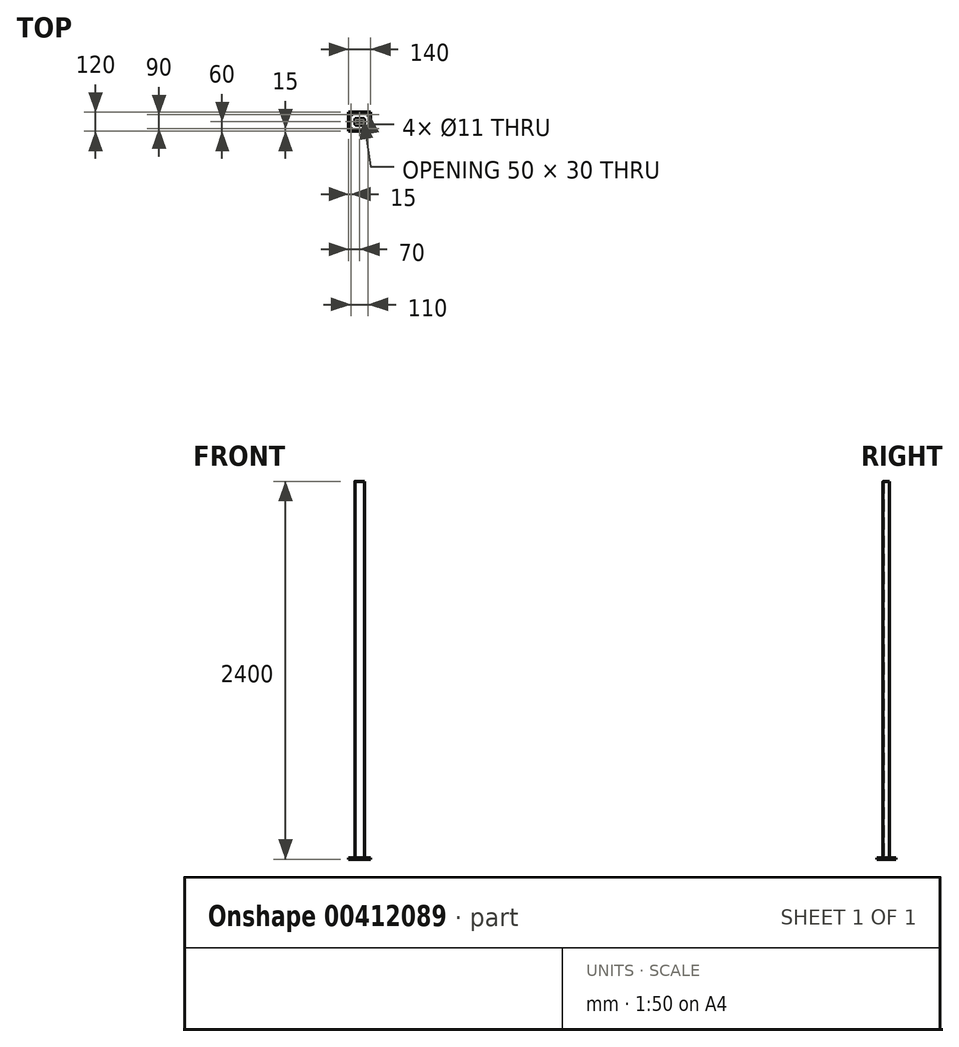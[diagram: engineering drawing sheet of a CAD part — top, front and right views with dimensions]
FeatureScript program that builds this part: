
annotation { "Feature Type Name" : "Feature", "Feature Type Description" : "" }
export const myFeature = defineFeature(function(context is Context, id is Id, definition is map)
    precondition{}
    {
        {
            var Q0;
            Q0=qCreatedBy(makeId("Top.planeOp"),FACE);
            var sketch = newSketch(context, id + "F0", { "sketchPlane" : qUnion([Q0])});
            skLineSegment(sketch, "E0.bottom", {"start": v(-70, 60) * mm, "end": v(70, 60) * mm});
            skLineSegment(sketch, "E0.top", {"start": v(-70, -60) * mm, "end": v(70, -60) * mm});
            skLineSegment(sketch, "E0.left", {"start": v(-70, 60) * mm, "end": v(-70, -60) * mm});
            skLineSegment(sketch, "E0.right", {"start": v(70, 60) * mm, "end": v(70, -60) * mm});
            skCircle(sketch, "E1", {"center": v(-55, 45) * mm, "radius": 5.5 * mm});
            skCircle(sketch, "E2", {"center": v(55, 45) * mm, "radius": 5.5 * mm});
            skCircle(sketch, "E3", {"center": v(-55, -45) * mm, "radius": 5.5 * mm});
            skCircle(sketch, "E4", {"center": v(55, -45) * mm, "radius": 5.5 * mm});
            skLineSegment(sketch, "E5.bottom", {"start": v(-25, 20) * mm, "end": v(25, 20) * mm});
            skLineSegment(sketch, "E5.top", {"start": v(-25, -20) * mm, "end": v(25, -20) * mm});
            skLineSegment(sketch, "E5.left", {"start": v(-30, 15) * mm, "end": v(-30, -15) * mm});
            skLineSegment(sketch, "E5.right", {"start": v(30, 15) * mm, "end": v(30, -15) * mm});
            skPoint(sketch, "E6.visualSharp", {"position": v(-30, 20) * mm});
            skArc(sketch, "E6.filletArc", {"start": v(-25, 20) * mm, "mid": v(-28.54, 18.54) * mm, "end": v(-30, 15) * mm});
            skPoint(sketch, "E7.visualSharp", {"position": v(30, 20) * mm});
            skArc(sketch, "E7.filletArc", {"start": v(30, 15) * mm, "mid": v(28.54, 18.54) * mm, "end": v(25, 20) * mm});
            skPoint(sketch, "E8.visualSharp", {"position": v(30, -20) * mm});
            skArc(sketch, "E8.filletArc", {"start": v(25, -20) * mm, "mid": v(28.54, -18.54) * mm, "end": v(30, -15) * mm});
            skPoint(sketch, "E9.visualSharp", {"position": v(-30, -20) * mm});
            skArc(sketch, "E9.filletArc", {"start": v(-30, -15) * mm, "mid": v(-28.54, -18.54) * mm, "end": v(-25, -20) * mm});
            skLineSegment(sketch, "E10.bottom", {"start": v(-20, 15) * mm, "end": v(20, 15) * mm});
            skLineSegment(sketch, "E10.top", {"start": v(-20, -15) * mm, "end": v(20, -15) * mm});
            skLineSegment(sketch, "E10.left", {"start": v(-25, 10) * mm, "end": v(-25, -10) * mm});
            skLineSegment(sketch, "E10.right", {"start": v(25, 10) * mm, "end": v(25, -10) * mm});
            skArc(sketch, "E11.filletArc", {"start": v(-20, 15) * mm, "mid": v(-23.54, 13.54) * mm, "end": v(-25, 10) * mm});
            skArc(sketch, "E12.filletArc", {"start": v(25, 10) * mm, "mid": v(23.54, 13.54) * mm, "end": v(20, 15) * mm});
            skArc(sketch, "E13.filletArc", {"start": v(20, -15) * mm, "mid": v(23.54, -13.54) * mm, "end": v(25, -10) * mm});
            skArc(sketch, "E14.filletArc", {"start": v(-25, -10) * mm, "mid": v(-23.54, -13.54) * mm, "end": v(-20, -15) * mm});
            skSolve(sketch);
        }
        {
            var Q0;
            Q0 = qSketchRegion(id + "F0", true);
            extrude(context, id + "F1", {"entities" : qUnion([Q0]), "depth" : 10 * mm});
        }
        {
            var Q0;
            Q0=makeQuery(id+"F0.imprint","IMPRINT",FACE,{"disambiguationData":[TD([[makeQuery(id+"F0.imprint","IMPRINT",EDGE,{"derivedFrom":sQuery(id+"F0.wireOp",EDGE,"E5.bottom")}),-1.0]])]});
            extrude(context, id + "F2", {"entities" : qUnion([Q0]), "operationType" : NewBodyOperationType.ADD, "depth" : 2400 * mm});
        }
    });
